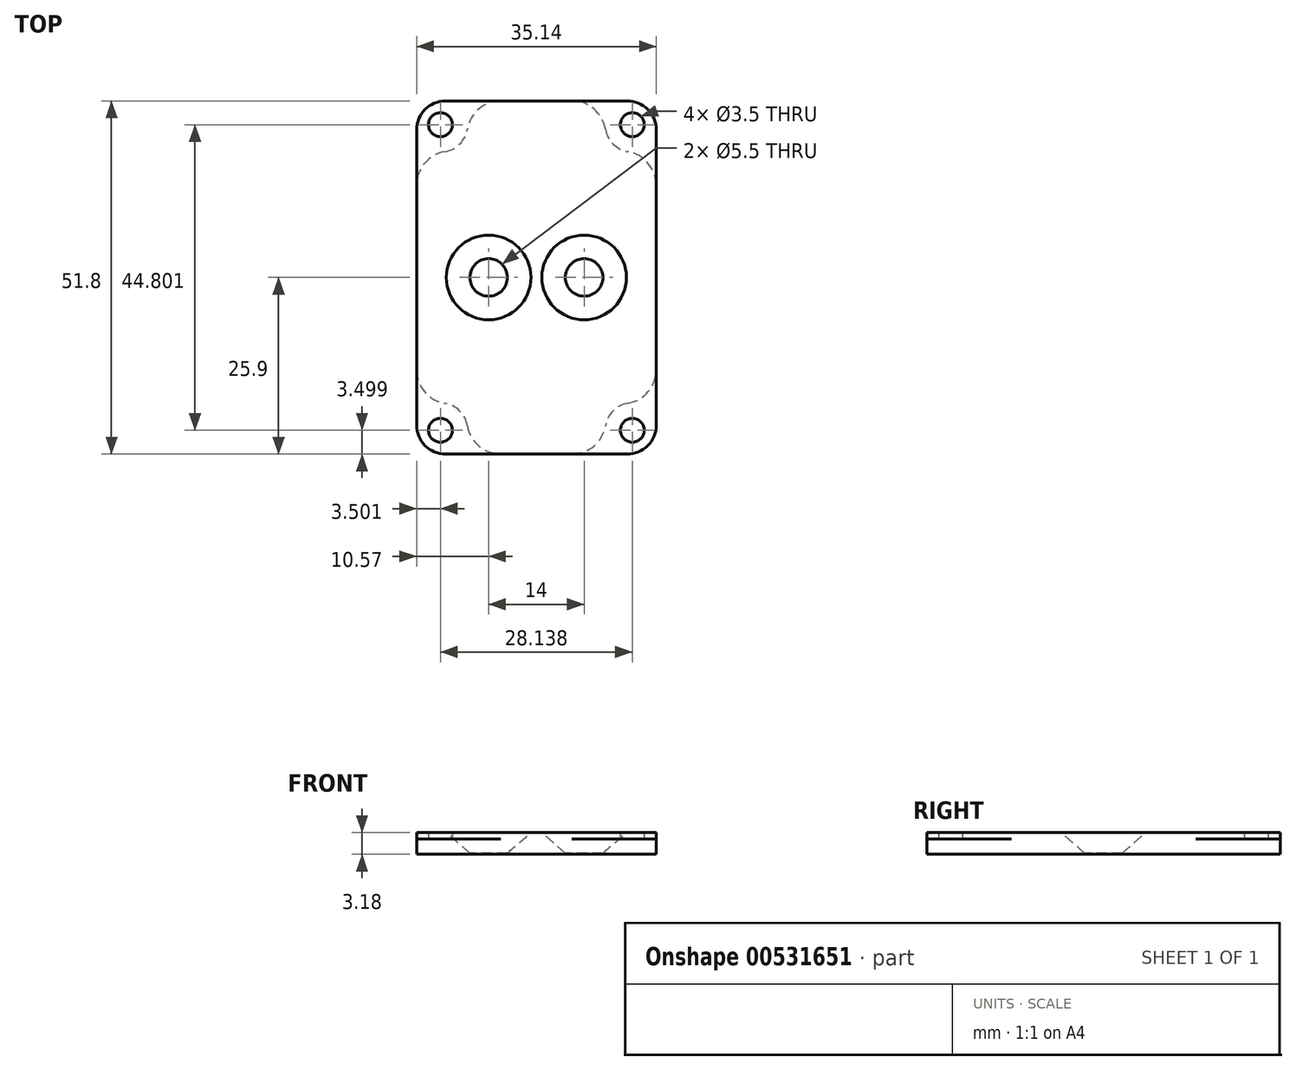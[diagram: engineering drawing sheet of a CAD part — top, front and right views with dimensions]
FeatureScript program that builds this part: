
annotation { "Feature Type Name" : "Feature", "Feature Type Description" : "" }
export const myFeature = defineFeature(function(context is Context, id is Id, definition is map)
    precondition{}
    {
        {
            var Q0;
            Q0=qCreatedBy(makeId("Top.planeOp"),FACE);
            var sketch = newSketch(context, id + "F0", { "sketchPlane" : qUnion([Q0])});
            skCircle(sketch, "E0", {"center": v(15, 23.88) * mm, "radius": 3.5 * mm, "construction": true});
            skCircle(sketch, "E1", {"center": v(-15, 23.88) * mm, "radius": 3.5 * mm, "construction": true});
            skCircle(sketch, "E2", {"center": v(-15, -23.88) * mm, "radius": 3.5 * mm, "construction": true});
            skCircle(sketch, "E3", {"center": v(15, -23.88) * mm, "radius": 3.5 * mm, "construction": true});
            skPoint(sketch, "E4.middle", {"position": v(0, 0) * mm});
            skCircle(sketch, "E5", {"center": v(-7, 0) * mm, "radius": 2.75 * mm});
            skCircle(sketch, "E6", {"center": v(7, 0) * mm, "radius": 2.75 * mm});
            skLineSegment(sketch, "E7", {"start": v(0, 9.32) * mm, "end": v(0, -9.78) * mm, "construction": true});
            skLineSegment(sketch, "E8", {"start": v(0, -9.78) * mm, "end": v(-12.82, 0) * mm, "construction": true});
            skLineSegment(sketch, "E9", {"start": v(-12.82, 0) * mm, "end": v(13.34, 0) * mm, "construction": true});
            skCircle(sketch, "E10", {"center": v(0, 0) * mm, "radius": 24.7 * mm, "construction": true});
            skCircle(sketch, "E11", {"center": v(-14.07, 22.4) * mm, "radius": 1.75 * mm});
            skCircle(sketch, "E12.MirrorC", {"center": v(14.07, 22.4) * mm, "radius": 1.75 * mm});
            skCircle(sketch, "E13.MirrorC", {"center": v(-14.07, -22.4) * mm, "radius": 1.75 * mm});
            skCircle(sketch, "E14.MirrorC", {"center": v(14.07, -22.4) * mm, "radius": 1.75 * mm});
            skLineSegment(sketch, "E15.bottom", {"start": v(13.32, 25.9) * mm, "end": v(-13.32, 25.9) * mm});
            skLineSegment(sketch, "E15.top", {"start": v(13.32, -25.9) * mm, "end": v(-13.32, -25.9) * mm});
            skLineSegment(sketch, "E15.left", {"start": v(17.57, 21.65) * mm, "end": v(17.57, -21.65) * mm});
            skLineSegment(sketch, "E15.right", {"start": v(-17.57, 21.65) * mm, "end": v(-17.57, -21.65) * mm});
            skPoint(sketch, "E16.visualSharp", {"position": v(-17.57, 25.9) * mm});
            skArc(sketch, "E16.filletArc", {"start": v(-13.32, 25.9) * mm, "mid": v(-16.32, 24.66) * mm, "end": v(-17.57, 21.65) * mm});
            skPoint(sketch, "E17.visualSharp", {"position": v(17.57, 25.9) * mm});
            skArc(sketch, "E17.filletArc", {"start": v(17.57, 21.65) * mm, "mid": v(16.32, 24.66) * mm, "end": v(13.32, 25.9) * mm});
            skPoint(sketch, "E18.visualSharp", {"position": v(17.57, -25.9) * mm});
            skArc(sketch, "E18.filletArc", {"start": v(13.32, -25.9) * mm, "mid": v(16.32, -24.66) * mm, "end": v(17.57, -21.65) * mm});
            skPoint(sketch, "E19.visualSharp", {"position": v(-17.57, -25.9) * mm});
            skArc(sketch, "E19.filletArc", {"start": v(-17.57, -21.65) * mm, "mid": v(-16.32, -24.66) * mm, "end": v(-13.32, -25.9) * mm});
            skSolve(sketch);
        }
        {
            var Q0;
            Q0 = qSketchRegion(id + "F0", true);
            extrude(context, id + "F1", {"entities" : qUnion([Q0]), "depth" : 3.17 * mm, "offsetDistance" : 25 * mm});
        }
        {
            var Q0;
            Q0=makeQuery(id+"F1.opExtrude","CAP_EDGE",EDGE,{"disambiguationData":[OSD([sQuery(id+"F0.wireOp",EDGE,"E5")])],"isStart":false});
            var Q1;
            Q1=makeQuery(id+"F1.opExtrude","CAP_EDGE",EDGE,{"disambiguationData":[OSD([sQuery(id+"F0.wireOp",EDGE,"E6")])],"isStart":false});
            chamfer(context, id + "F2", {"entities" : qUnion([Q0, Q1]), "chamferType" : ChamferType.OFFSET_ANGLE, "width" : 3 * mm, "oppositeDirection" : false, "angle" : 49 * degree, "tangentPropagation" : true});
        }
        {
            var Q0;
            Q0=makeQuery(id+"F1.opExtrude","CAP_FACE",FACE,{"disambiguationData":[OSD([sQuery(id+"F0.wireOp",EDGE,"E5"),sQuery(id+"F0.wireOp",EDGE,"E6"),sQuery(id+"F0.wireOp",EDGE,"E11"),sQuery(id+"F0.wireOp",EDGE,"E12.MirrorC"),sQuery(id+"F0.wireOp",EDGE,"E13.MirrorC"),sQuery(id+"F0.wireOp",EDGE,"E14.MirrorC"),sQuery(id+"F0.wireOp",EDGE,"E15.bottom"),sQuery(id+"F0.wireOp",EDGE,"E15.top"),sQuery(id+"F0.wireOp",EDGE,"E15.left"),sQuery(id+"F0.wireOp",EDGE,"E15.right"),sQuery(id+"F0.wireOp",EDGE,"E16.filletArc"),sQuery(id+"F0.wireOp",EDGE,"E17.filletArc"),sQuery(id+"F0.wireOp",EDGE,"E18.filletArc"),sQuery(id+"F0.wireOp",EDGE,"E19.filletArc")])],"isStart":true});
            var sketch = newSketch(context, id + "F3", { "sketchPlane" : qUnion([Q0])});
            skCircle(sketch, "E20", {"center": v(-14.07, 22.4) * mm, "radius": 4 * mm});
            skCircle(sketch, "E21", {"center": v(14.07, 22.4) * mm, "radius": 4 * mm});
            skCircle(sketch, "E22", {"center": v(-14.07, -22.4) * mm, "radius": 4 * mm});
            skCircle(sketch, "E23", {"center": v(14.07, -22.4) * mm, "radius": 4 * mm});
            skSolve(sketch);
        }
        {
            var Q0;
            Q0 = qSketchRegion(id + "F3", true);
            extrude(context, id + "F4", {"entities" : qUnion([Q0]), "operationType" : NewBodyOperationType.REMOVE, "oppositeDirection" : true, "depth" : 2.25 * mm, "offsetDistance" : 25 * mm});
        }
        {
            var Q0;
            Q0=makeQuery(id+"F4.boolean.opBoolean","INTERSECT",EDGE,{"derivedFrom":[makeQuery(id+"F1.opExtrude","SWEPT_FACE",FACE,{"disambiguationData":[OSD([sQuery(id+"F0.wireOp",EDGE,"E15.top")])]}),makeQuery(id+"F4.opExtrude","SWEPT_FACE",FACE,{"disambiguationData":[OSD([sQuery(id+"F3.wireOp",EDGE,"E20")])]})]});
            var Q1;
            Q1=makeQuery(id+"F4.boolean.opBoolean","INTERSECT",EDGE,{"derivedFrom":[makeQuery(id+"F1.opExtrude","SWEPT_FACE",FACE,{"disambiguationData":[OSD([sQuery(id+"F0.wireOp",EDGE,"E15.right")])]}),makeQuery(id+"F4.opExtrude","SWEPT_FACE",FACE,{"disambiguationData":[OSD([sQuery(id+"F3.wireOp",EDGE,"E20")])]})]});
            var Q2;
            Q2=makeQuery(id+"F4.boolean.opBoolean","INTERSECT",EDGE,{"derivedFrom":[makeQuery(id+"F1.opExtrude","SWEPT_FACE",FACE,{"disambiguationData":[OSD([sQuery(id+"F0.wireOp",EDGE,"E15.top")])]}),makeQuery(id+"F4.opExtrude","SWEPT_FACE",FACE,{"disambiguationData":[OSD([sQuery(id+"F3.wireOp",EDGE,"E21")])]})]});
            var Q3;
            Q3=makeQuery(id+"F4.boolean.opBoolean","INTERSECT",EDGE,{"derivedFrom":[makeQuery(id+"F1.opExtrude","SWEPT_FACE",FACE,{"disambiguationData":[OSD([sQuery(id+"F0.wireOp",EDGE,"E15.left")])]}),makeQuery(id+"F4.opExtrude","SWEPT_FACE",FACE,{"disambiguationData":[OSD([sQuery(id+"F3.wireOp",EDGE,"E21")])]})]});
            var Q4;
            Q4=makeQuery(id+"F4.boolean.opBoolean","INTERSECT",EDGE,{"derivedFrom":[makeQuery(id+"F1.opExtrude","SWEPT_FACE",FACE,{"disambiguationData":[OSD([sQuery(id+"F0.wireOp",EDGE,"E15.right")])]}),makeQuery(id+"F4.opExtrude","SWEPT_FACE",FACE,{"disambiguationData":[OSD([sQuery(id+"F3.wireOp",EDGE,"E22")])]})]});
            var Q5;
            Q5=makeQuery(id+"F4.boolean.opBoolean","INTERSECT",EDGE,{"derivedFrom":[makeQuery(id+"F1.opExtrude","SWEPT_FACE",FACE,{"disambiguationData":[OSD([sQuery(id+"F0.wireOp",EDGE,"E15.bottom")])]}),makeQuery(id+"F4.opExtrude","SWEPT_FACE",FACE,{"disambiguationData":[OSD([sQuery(id+"F3.wireOp",EDGE,"E22")])]})]});
            var Q6;
            Q6=makeQuery(id+"F4.boolean.opBoolean","INTERSECT",EDGE,{"derivedFrom":[makeQuery(id+"F1.opExtrude","SWEPT_FACE",FACE,{"disambiguationData":[OSD([sQuery(id+"F0.wireOp",EDGE,"E15.bottom")])]}),makeQuery(id+"F4.opExtrude","SWEPT_FACE",FACE,{"disambiguationData":[OSD([sQuery(id+"F3.wireOp",EDGE,"E23")])]})]});
            var Q7;
            Q7=makeQuery(id+"F4.boolean.opBoolean","INTERSECT",EDGE,{"derivedFrom":[makeQuery(id+"F1.opExtrude","SWEPT_FACE",FACE,{"disambiguationData":[OSD([sQuery(id+"F0.wireOp",EDGE,"E15.left")])]}),makeQuery(id+"F4.opExtrude","SWEPT_FACE",FACE,{"disambiguationData":[OSD([sQuery(id+"F3.wireOp",EDGE,"E23")])]})]});
            fillet(context, id + "F5", {"entities" : qUnion([Q0, Q1, Q2, Q3, Q4, Q5, Q6, Q7]), "radius" : 5 * mm, "tangentPropagation" : true, "allowEdgeOverflow" : false});
        }
    });
